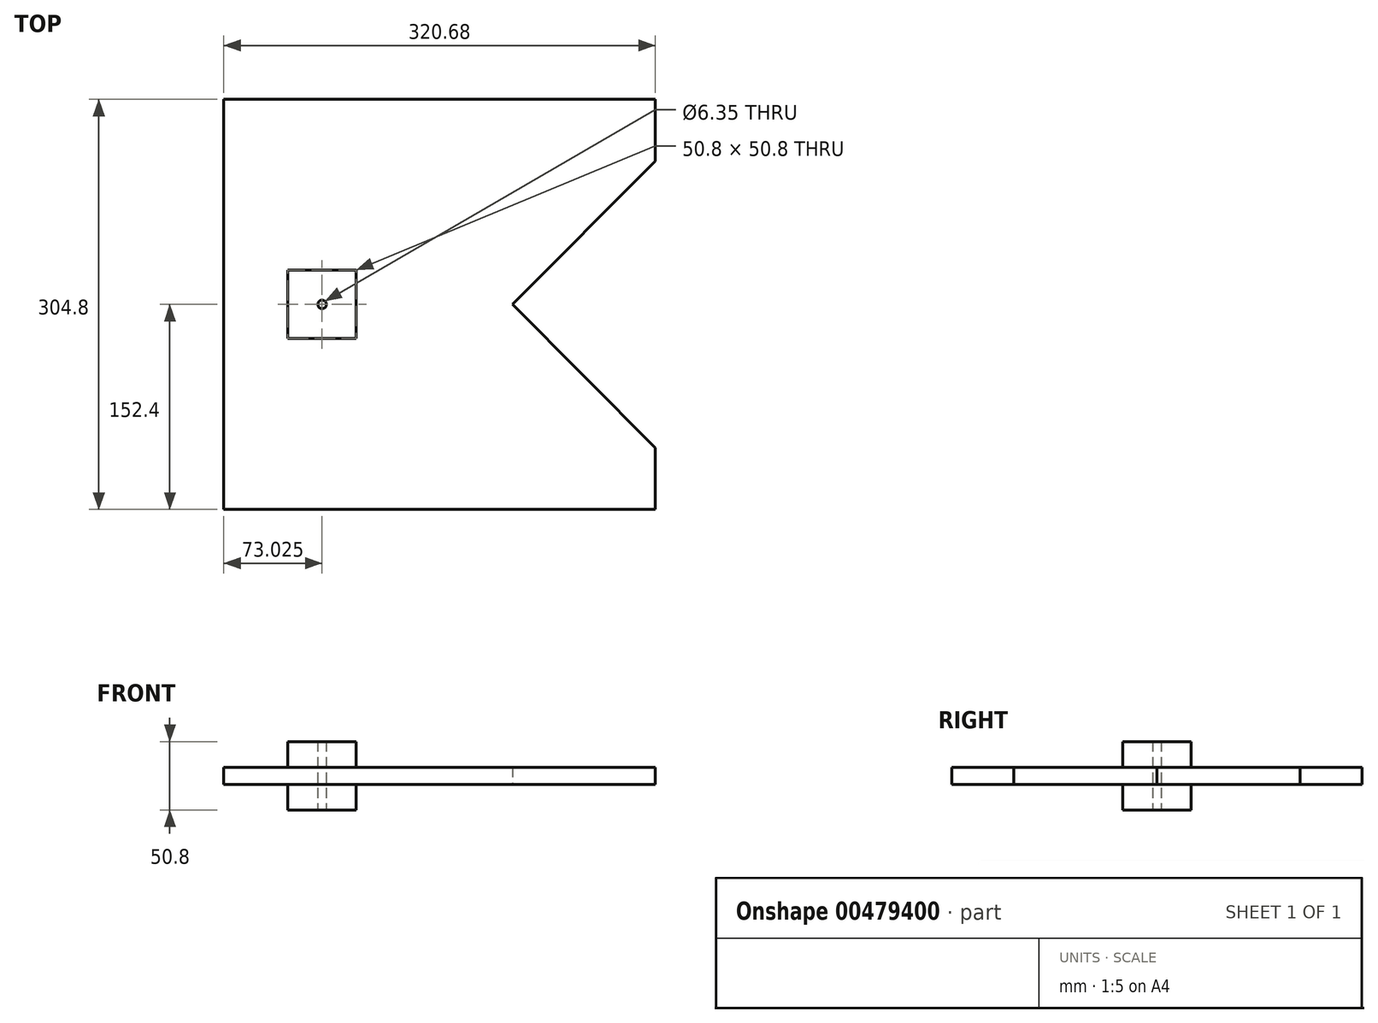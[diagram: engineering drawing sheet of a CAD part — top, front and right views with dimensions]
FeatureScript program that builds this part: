
annotation { "Feature Type Name" : "Feature", "Feature Type Description" : "" }
export const myFeature = defineFeature(function(context is Context, id is Id, definition is map)
    precondition{}
    {
        {
            var Q0;
            Q0=qCreatedBy(makeId("Top.planeOp"),FACE);
            var sketch = newSketch(context, id + "F0", { "sketchPlane" : qUnion([Q0])});
            skLineSegment(sketch, "E0.bottom", {"start": v(0, 0) * mm, "end": v(320.68, 0) * mm});
            skLineSegment(sketch, "E0.top", {"start": v(0, 304.8) * mm, "end": v(320.68, 304.8) * mm});
            skLineSegment(sketch, "E0.left", {"start": v(0, 0) * mm, "end": v(0, 304.8) * mm});
            skLineSegment(sketch, "E0.right", {"start": v(320.68, 0) * mm, "end": v(320.68, 304.8) * mm});
            skLineSegment(sketch, "E1", {"start": v(320.68, 152.34) * mm, "end": v(214.35, 152.34) * mm});
            skLineSegment(sketch, "E2", {"start": v(214.35, 152.34) * mm, "end": v(320.68, 258.78) * mm});
            skLineSegment(sketch, "E3", {"start": v(214.35, 152.34) * mm, "end": v(320.68, 45.9) * mm});
            skLineSegment(sketch, "E4.bottom", {"start": v(47.62, 127) * mm, "end": v(98.42, 127) * mm});
            skLineSegment(sketch, "E4.top", {"start": v(47.62, 177.8) * mm, "end": v(98.42, 177.8) * mm});
            skLineSegment(sketch, "E4.left", {"start": v(47.62, 127) * mm, "end": v(47.62, 177.8) * mm});
            skLineSegment(sketch, "E4.right", {"start": v(98.42, 127) * mm, "end": v(98.42, 177.8) * mm});
            skCircle(sketch, "E5", {"center": v(73.02, 152.4) * mm, "radius": 3.18 * mm});
            skSolve(sketch);
        }
        {
            var Q0;
            {var subQ4=sQuery(id+"F0.wireOp",EDGE,"E0.bottom");Q0=makeQuery(id+"F0.imprint","IMPRINT",FACE,{"disambiguationData":[TD([[makeQuery(id+"F0.imprint","IMPRINT",EDGE,{"derivedFrom":subQ4}),1.0]])]});}
            var Q1;
            Q1=makeQuery(id+"F0.imprint","IMPRINT",FACE,{"disambiguationData":[TD([[makeQuery(id+"F0.imprint","IMPRINT",EDGE,{"derivedFrom":sQuery(id+"F0.wireOp",EDGE,"E4.bottom")}),1.0]])]});
            extrude(context, id + "F1", {"entities" : qUnion([Q0, Q1]), "depth" : 12.7 * mm, "offsetDistance" : 25.4 * mm});
        }
        {
            var Q0;
            Q0=makeQuery(id+"F0.imprint","IMPRINT",FACE,{"disambiguationData":[TD([[makeQuery(id+"F0.imprint","IMPRINT",EDGE,{"derivedFrom":sQuery(id+"F0.wireOp",EDGE,"E4.bottom")}),1.0]])]});
            extrude(context, id + "F2", {"entities" : qUnion([Q0]), "operationType" : NewBodyOperationType.ADD, "depth" : 31.75 * mm, "offsetDistance" : 25.4 * mm});
        }
        {
            var Q0;
            Q0=makeQuery(id+"F0.imprint","IMPRINT",FACE,{"disambiguationData":[TD([[makeQuery(id+"F0.imprint","IMPRINT",EDGE,{"derivedFrom":sQuery(id+"F0.wireOp",EDGE,"E4.bottom")}),1.0]])]});
            extrude(context, id + "F3", {"entities" : qUnion([Q0]), "operationType" : NewBodyOperationType.ADD, "oppositeDirection" : true, "depth" : 19.05 * mm, "offsetDistance" : 25.4 * mm});
        }
    });
